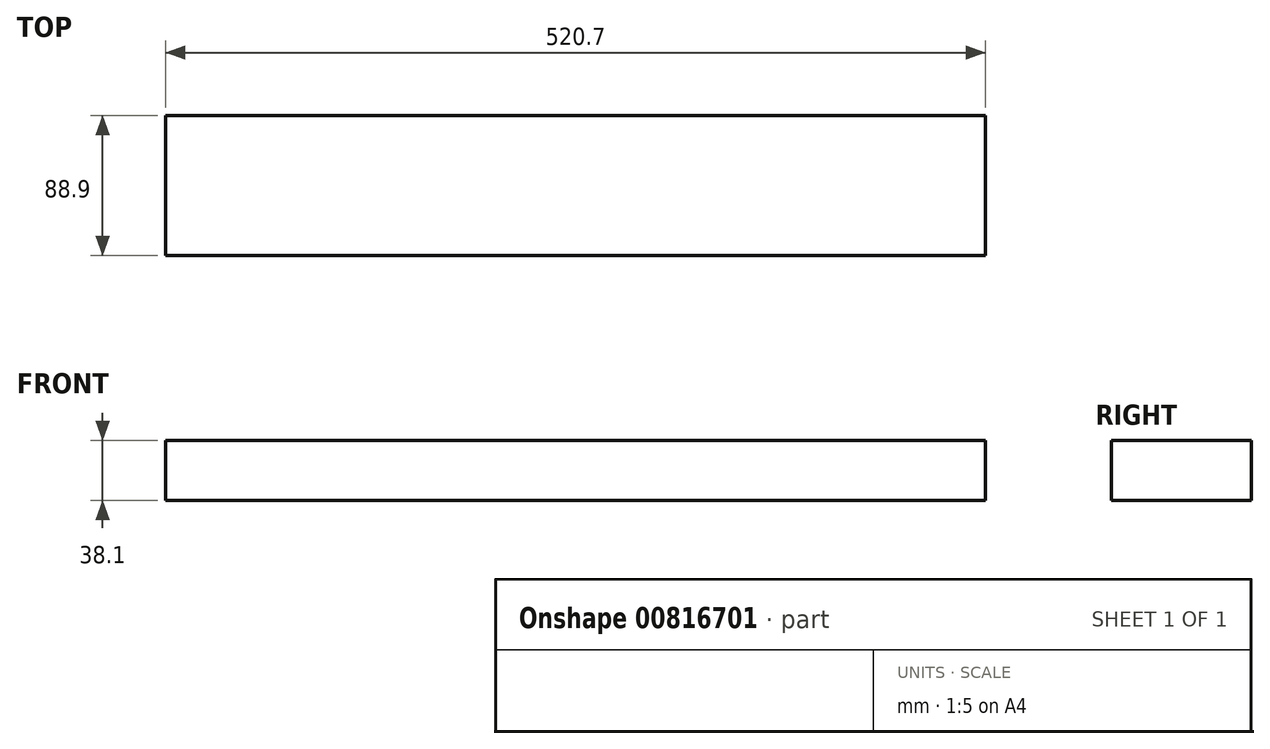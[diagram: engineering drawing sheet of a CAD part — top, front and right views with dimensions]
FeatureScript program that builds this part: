
annotation { "Feature Type Name" : "Feature", "Feature Type Description" : "" }
export const myFeature = defineFeature(function(context is Context, id is Id, definition is map)
    precondition{}
    {
        {
            var Q0;
            Q0=qCreatedBy(makeId("Top.planeOp"),FACE);
            var sketch = newSketch(context, id + "F0", { "sketchPlane" : qUnion([Q0])});
            skLineSegment(sketch, "E0.bottom", {"start": v(0, 0) * mm, "end": v(520.7, 0) * mm});
            skLineSegment(sketch, "E0.top", {"start": v(0, 88.9) * mm, "end": v(520.7, 88.9) * mm});
            skLineSegment(sketch, "E0.left", {"start": v(0, 0) * mm, "end": v(0, 88.9) * mm});
            skLineSegment(sketch, "E0.right", {"start": v(520.7, 0) * mm, "end": v(520.7, 88.9) * mm});
            skSolve(sketch);
        }
        {
            var Q0;
            Q0 = qSketchRegion(id + "F0", true);
            extrude(context, id + "F1", {"entities" : qUnion([Q0]), "depth" : 38.1 * mm, "offsetDistance" : 25.4 * mm});
        }
    });
